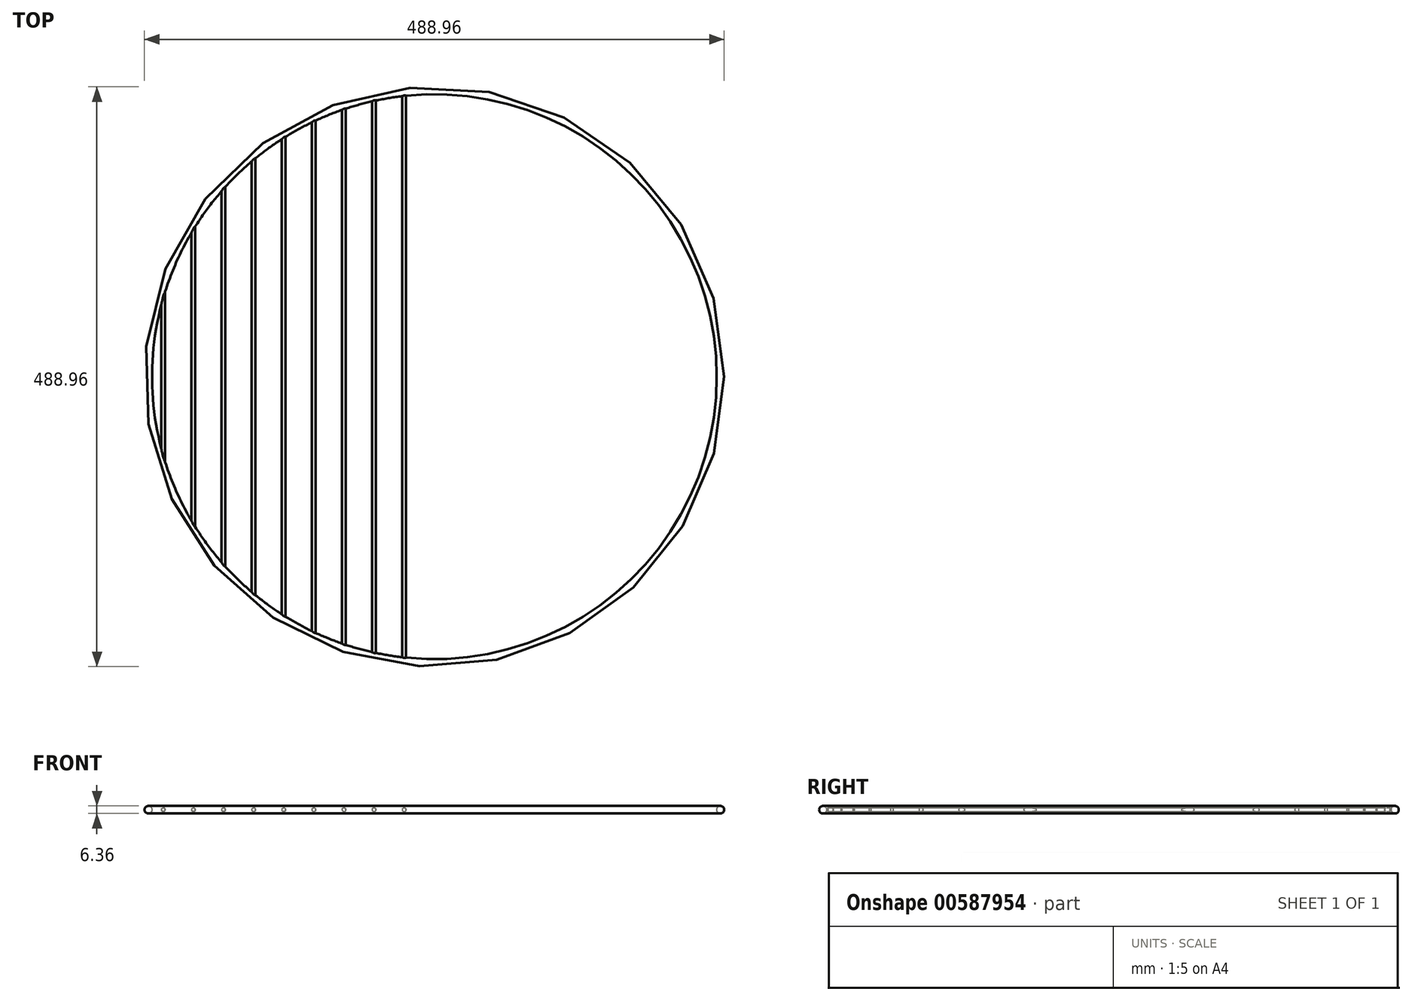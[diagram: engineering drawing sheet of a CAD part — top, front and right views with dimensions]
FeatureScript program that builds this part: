
annotation { "Feature Type Name" : "Feature", "Feature Type Description" : "" }
export const myFeature = defineFeature(function(context is Context, id is Id, definition is map)
    precondition{}
    {
        {
            var Q0;
            Q0=qCreatedBy(makeId("Front.planeOp"),FACE);
            var sketch = newSketch(context, id + "F0", { "sketchPlane" : qUnion([Q0])});
            skCircle(sketch, "E0", {"center": v(241.3, 0) * mm, "radius": 3.18 * mm});
            skLineSegment(sketch, "E1", {"start": v(0, 0) * mm, "end": v(0, 32.12) * mm, "construction": true});
            skSolve(sketch);
        }
        {
            var Q0;
            Q0=qCreatedBy(makeId("Front.planeOp"),FACE);
            var sketch = newSketch(context, id + "F1", { "sketchPlane" : qUnion([Q0])});
            skCircle(sketch, "E2", {"center": v(0, 0) * mm, "radius": 1.59 * mm});
            skCircle(sketch, "E3.1.0.0", {"center": v(-25.4, 0) * mm, "radius": 1.59 * mm});
            skCircle(sketch, "E3.2.0.0", {"center": v(-50.8, 0) * mm, "radius": 1.59 * mm});
            skCircle(sketch, "E3.3.0.0", {"center": v(-76.2, 0) * mm, "radius": 1.59 * mm});
            skCircle(sketch, "E3.4.0.0", {"center": v(-101.6, 0) * mm, "radius": 1.59 * mm});
            skLineSegment(sketch, "E3.direction1", {"start": v(0, 0) * mm, "end": v(-25.4, 0) * mm, "construction": true});
            skCircle(sketch, "E4.0.5.0", {"center": v(-127, 0) * mm, "radius": 1.59 * mm});
            skCircle(sketch, "E4.0.6.0", {"center": v(-152.4, 0) * mm, "radius": 1.59 * mm});
            skCircle(sketch, "E4.0.7.0", {"center": v(-177.8, 0) * mm, "radius": 1.59 * mm});
            skCircle(sketch, "E4.0.8.0", {"center": v(-203.2, 0) * mm, "radius": 1.59 * mm});
            skCircle(sketch, "E4.0.9.0", {"center": v(-228.6, 0) * mm, "radius": 1.59 * mm});
            skLineSegment(sketch, "E5.MirrorCS", {"start": v(0, 0) * mm, "end": v(25.4, 0) * mm, "construction": true});
            skCircle(sketch, "E6.MirrorC", {"center": v(25.4, 0) * mm, "radius": 1.59 * mm});
            skCircle(sketch, "E7.MirrorC", {"center": v(127, 0) * mm, "radius": 1.59 * mm});
            skCircle(sketch, "E8.MirrorC", {"center": v(101.6, 0) * mm, "radius": 1.59 * mm});
            skCircle(sketch, "E9.MirrorC", {"center": v(76.2, 0) * mm, "radius": 1.59 * mm});
            skCircle(sketch, "E10.MirrorC", {"center": v(50.8, 0) * mm, "radius": 1.59 * mm});
            skCircle(sketch, "E11.MirrorC", {"center": v(203.2, 0) * mm, "radius": 1.59 * mm});
            skCircle(sketch, "E12.MirrorC", {"center": v(228.6, 0) * mm, "radius": 1.59 * mm});
            skCircle(sketch, "E13.MirrorC", {"center": v(177.8, 0) * mm, "radius": 1.59 * mm});
            skCircle(sketch, "E14.MirrorC", {"center": v(152.4, 0) * mm, "radius": 1.59 * mm});
            skSolve(sketch);
        }
        {
            var Q0;
            Q0=makeQuery(id+"F0.imprint","IMPRINT",FACE,{"disambiguationData":[TD([[makeQuery(id+"F0.imprint","IMPRINT",EDGE,{"derivedFrom":sQuery(id+"F0.wireOp",EDGE,"E0")}),1.0]])]});
            var Q1;
            Q1=sQuery(id+"F0.wireOp",EDGE,"E1");
            revolve(context, id + "F2", {"entities" : qUnion([Q0]), "axis" : qUnion([Q1]), "revolveType" : RevolveType.FULL});
        }
        {
            var Q0;
            Q0=makeQuery(id+"F1.imprint","IMPRINT",FACE,{"disambiguationData":[TD([[makeQuery(id+"F1.imprint","IMPRINT",EDGE,{"derivedFrom":sQuery(id+"F1.wireOp",EDGE,"E4.0.9.0")}),1.0]])]});
            var Q1;
            Q1=makeQuery(id+"F1.imprint","IMPRINT",FACE,{"disambiguationData":[TD([[makeQuery(id+"F1.imprint","IMPRINT",EDGE,{"derivedFrom":sQuery(id+"F1.wireOp",EDGE,"E4.0.8.0")}),1.0]])]});
            var Q2;
            Q2=makeQuery(id+"F1.imprint","IMPRINT",FACE,{"disambiguationData":[TD([[makeQuery(id+"F1.imprint","IMPRINT",EDGE,{"derivedFrom":sQuery(id+"F1.wireOp",EDGE,"E4.0.7.0")}),1.0]])]});
            var Q3;
            Q3=makeQuery(id+"F1.imprint","IMPRINT",FACE,{"disambiguationData":[TD([[makeQuery(id+"F1.imprint","IMPRINT",EDGE,{"derivedFrom":sQuery(id+"F1.wireOp",EDGE,"E4.0.6.0")}),1.0]])]});
            var Q4;
            Q4=makeQuery(id+"F1.imprint","IMPRINT",FACE,{"disambiguationData":[TD([[makeQuery(id+"F1.imprint","IMPRINT",EDGE,{"derivedFrom":sQuery(id+"F1.wireOp",EDGE,"E4.0.5.0")}),1.0]])]});
            var Q5;
            Q5=makeQuery(id+"F1.imprint","IMPRINT",FACE,{"disambiguationData":[TD([[makeQuery(id+"F1.imprint","IMPRINT",EDGE,{"derivedFrom":sQuery(id+"F1.wireOp",EDGE,"E3.4.0.0")}),1.0]])]});
            var Q6;
            Q6=makeQuery(id+"F1.imprint","IMPRINT",FACE,{"disambiguationData":[TD([[makeQuery(id+"F1.imprint","IMPRINT",EDGE,{"derivedFrom":sQuery(id+"F1.wireOp",EDGE,"E3.3.0.0")}),1.0]])]});
            var Q7;
            Q7=makeQuery(id+"F1.imprint","IMPRINT",FACE,{"disambiguationData":[TD([[makeQuery(id+"F1.imprint","IMPRINT",EDGE,{"derivedFrom":sQuery(id+"F1.wireOp",EDGE,"E3.2.0.0")}),1.0]])]});
            var Q8;
            Q8=makeQuery(id+"F1.imprint","IMPRINT",FACE,{"disambiguationData":[TD([[makeQuery(id+"F1.imprint","IMPRINT",EDGE,{"derivedFrom":sQuery(id+"F1.wireOp",EDGE,"E3.1.0.0")}),1.0]])]});
            var Q9;
            Q9=makeQuery(id+"F1.imprint","IMPRINT",FACE,{"disambiguationData":[TD([[makeQuery(id+"F1.imprint","IMPRINT",EDGE,{"derivedFrom":sQuery(id+"F1.wireOp",EDGE,"E2")}),-1.0]])]});
            var Q10;
            Q10=makeQuery(id+"F1.imprint","IMPRINT",FACE,{"disambiguationData":[TD([[makeQuery(id+"F1.imprint","IMPRINT",EDGE,{"derivedFrom":sQuery(id+"F1.wireOp",EDGE,"E6.MirrorC")}),-1.0]])]});
            var Q11;
            Q11=makeQuery(id+"F1.imprint","IMPRINT",FACE,{"disambiguationData":[TD([[makeQuery(id+"F1.imprint","IMPRINT",EDGE,{"derivedFrom":sQuery(id+"F1.wireOp",EDGE,"E10.MirrorC")}),-1.0]])]});
            var Q12;
            Q12=makeQuery(id+"F1.imprint","IMPRINT",FACE,{"disambiguationData":[TD([[makeQuery(id+"F1.imprint","IMPRINT",EDGE,{"derivedFrom":sQuery(id+"F1.wireOp",EDGE,"E9.MirrorC")}),-1.0]])]});
            var Q13;
            Q13=makeQuery(id+"F1.imprint","IMPRINT",FACE,{"disambiguationData":[TD([[makeQuery(id+"F1.imprint","IMPRINT",EDGE,{"derivedFrom":sQuery(id+"F1.wireOp",EDGE,"E8.MirrorC")}),-1.0]])]});
            var Q14;
            Q14=makeQuery(id+"F1.imprint","IMPRINT",FACE,{"disambiguationData":[TD([[makeQuery(id+"F1.imprint","IMPRINT",EDGE,{"derivedFrom":sQuery(id+"F1.wireOp",EDGE,"E7.MirrorC")}),-1.0]])]});
            var Q15;
            Q15=makeQuery(id+"F1.imprint","IMPRINT",FACE,{"disambiguationData":[TD([[makeQuery(id+"F1.imprint","IMPRINT",EDGE,{"derivedFrom":sQuery(id+"F1.wireOp",EDGE,"E14.MirrorC")}),-1.0]])]});
            var Q16;
            Q16=makeQuery(id+"F1.imprint","IMPRINT",FACE,{"disambiguationData":[TD([[makeQuery(id+"F1.imprint","IMPRINT",EDGE,{"derivedFrom":sQuery(id+"F1.wireOp",EDGE,"E13.MirrorC")}),-1.0]])]});
            var Q17;
            Q17=makeQuery(id+"F1.imprint","IMPRINT",FACE,{"disambiguationData":[TD([[makeQuery(id+"F1.imprint","IMPRINT",EDGE,{"derivedFrom":sQuery(id+"F1.wireOp",EDGE,"E11.MirrorC")}),-1.0]])]});
            var Q18;
            Q18=makeQuery(id+"F1.imprint","IMPRINT",FACE,{"disambiguationData":[TD([[makeQuery(id+"F1.imprint","IMPRINT",EDGE,{"derivedFrom":sQuery(id+"F1.wireOp",EDGE,"E12.MirrorC")}),-1.0]])]});
            extrude(context, id + "F3", {"entities" : qUnion([Q0, Q1, Q2, Q3, Q4, Q5, Q6, Q7, Q8, Q9, Q10, Q11, Q12, Q13, Q14, Q15, Q16, Q17, Q18]), "operationType" : NewBodyOperationType.ADD, "endBound" : BoundingType.UP_TO_NEXT, "depth" : 25.4 * mm, "offsetDistance" : 25.4 * mm, "hasSecondDirection" : true, "secondDirectionBound" : SecondDirectionBoundingType.UP_TO_NEXT, "secondDirectionOppositeDirection" : true, "secondDirectionDepth" : 25.4 * mm});
        }
    });
